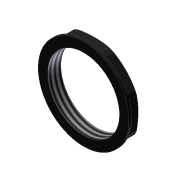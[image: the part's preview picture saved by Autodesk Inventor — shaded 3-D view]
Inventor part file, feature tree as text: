
AUTODESK INVENTOR PART (.ipt)
format: ipt  version: unknown  size: 195,072 bytes
history: native  units: mm
features: imported_body x1, thread x1
ambient origin geometry x8: Origin, YZ Plane, XZ Plane, XY Plane, X Axis, Y Axis, Z Axis, Center Point
feature tree (2):
  imported_body  "Base1"
  thread  "Thread1"  [1 undecoded]
note: 1 required parameter value undecoded (feature->parameter linkage not recoverable at this tier; creation-order binding heuristic only, values carry confidence <= 0.55)
